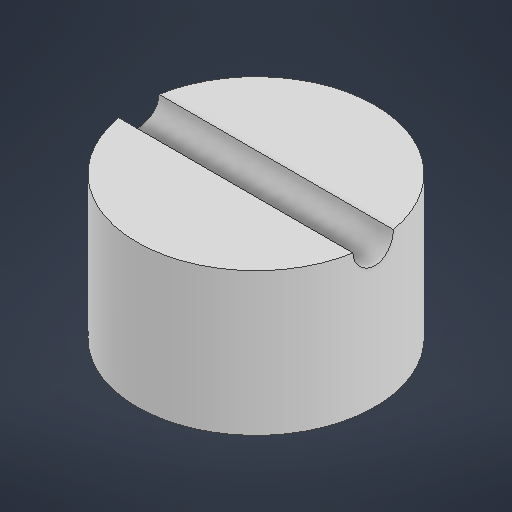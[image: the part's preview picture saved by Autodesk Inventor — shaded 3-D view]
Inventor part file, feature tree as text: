
AUTODESK INVENTOR PART (.ipt)
format: ipt  version: 2025.3 (Build 293356000, 356)  size: 192,000 bytes
history: native  units: mm
features: extrude x3, sketch x2
ambient origin geometry x8: Origin, YZ Plane, XZ Plane, XY Plane, X Axis, Y Axis, Z Axis, Center Point
bodies: Solid1 (feature_tree)
feature tree (5):
  sketch  "Sketch1"  dims[d0=10.0mm d1=8.5mm]
  extrude  "Extrusion1"  Depth=10.0mm
  extrude  "Extrusion2"  Depth=10.0mm TaperAngle=0.0deg
  extrude  "Extrusion4"  Depth=10.0mm
  sketch  "Sketch3"  dims[d2=6.0mm d3=0.0mm d4=2.0mm d5=0.0mm d9=1.7mm d10=5.0mm d11=10.0mm d12=0.0mm]
